# Revit family: TD92_CON719_AMA000_RVT20_R00
name_source: partatom
category: Mobiliário
units: mm (PartAtom-declared; Revit-internal decimal feet)

## family parameters
Com base no plano de trabalho = Não
Compartilhado = Não
Corte com vazios quando carregada = Não
Número OmniClass = 23.40.20.00
Ponto de cálculo do ambiente = Não
Sempre na vertical = Sim
Título OmniClass = General Furniture and Specialties

## types (1)
- TD92_CON719_AMA000_RVT20_R00
    Descrição = Para aquela hora especial e muito criativa do dia das crianças, à Mesa Infantil Tramontina Cona em Polietileno é a companhia perfeita! Ela vai ajudar seus pequenos a desenharem, pintarem e modelarem suas massinhas com muito mais disposição e descontração, pois possui uma cor vibrante e um design pensado especialmente nos pequenos. Ela ainda é fabricada em material livre de toxinas e é a escolha perfeita para o quarto ou playgrounds de casas ou condomínios.
    Elevação padrão = 0  [stored 0 ft]
    Fabricante = Tramontina Delta S/A
    Modelo = Mesa de Centro Infantil Tramontina Cona em Polietileno Amarelo
    Nota-chave = 92719000
    URL = https://www.tramontinastore.com

note: [stored X ft] marks values corroborated as IEEE doubles in the binary element streams (Revit-internal decimal feet)
